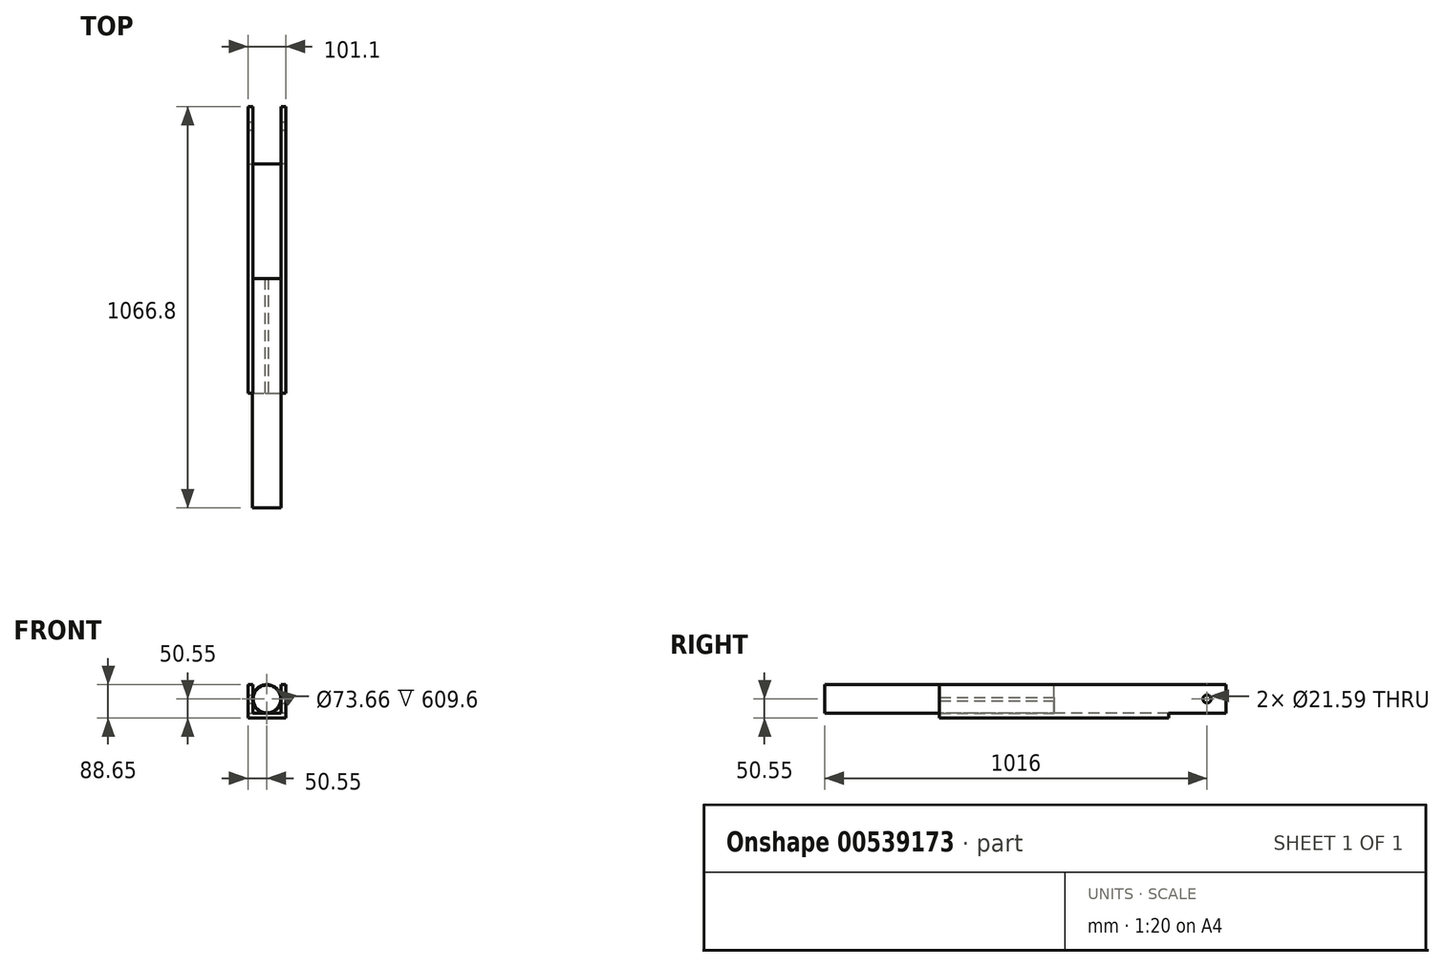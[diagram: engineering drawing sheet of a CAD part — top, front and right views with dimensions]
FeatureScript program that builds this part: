
annotation { "Feature Type Name" : "Feature", "Feature Type Description" : "" }
export const myFeature = defineFeature(function(context is Context, id is Id, definition is map)
    precondition{}
    {
        {
            var Q0;
            Q0=qCreatedBy(makeId("Front.planeOp"),FACE);
            var sketch = newSketch(context, id + "F0", { "sketchPlane" : qUnion([Q0])});
            skCircle(sketch, "E0", {"center": v(0, 0) * mm, "radius": 38.1 * mm});
            skCircle(sketch, "E1", {"center": v(0, 0) * mm, "radius": 36.83 * mm});
            skSolve(sketch);
        }
        {
            var Q0;
            Q0 = qSketchRegion(id + "F0", true);
            extrude(context, id + "F1", {"entities" : qUnion([Q0]), "depth" : 609.6 * mm, "offsetDistance" : 25.4 * mm});
        }
        {
            var Q0;
            Q0=qCreatedBy(makeId("Front.planeOp"),FACE);
            var sketch = newSketch(context, id + "F2", { "sketchPlane" : qUnion([Q0])});
            skLineSegment(sketch, "E2.bottom", {"start": v(-50.55, 38.1) * mm, "end": v(-37.85, 38.1) * mm});
            skLineSegment(sketch, "E2.top", {"start": v(-50.55, -38.1) * mm, "end": v(-37.85, -38.1) * mm});
            skLineSegment(sketch, "E2.left", {"start": v(-50.55, 38.1) * mm, "end": v(-50.55, -38.1) * mm});
            skLineSegment(sketch, "E2.right", {"start": v(-37.85, 38.1) * mm, "end": v(-37.85, -38.1) * mm});
            skLineSegment(sketch, "E3.MirrorCS", {"start": v(37.85, 38.1) * mm, "end": v(37.85, -38.1) * mm});
            skLineSegment(sketch, "E4.MirrorCS", {"start": v(50.55, 38.1) * mm, "end": v(50.55, -38.1) * mm});
            skLineSegment(sketch, "E5.MirrorCS", {"start": v(50.55, 38.1) * mm, "end": v(37.85, 38.1) * mm});
            skLineSegment(sketch, "E6.MirrorCS", {"start": v(50.55, -38.1) * mm, "end": v(37.85, -38.1) * mm});
            skLineSegment(sketch, "E7.bottom", {"start": v(-50.55, -38.1) * mm, "end": v(51.05, -38.1) * mm});
            skLineSegment(sketch, "E7.left", {"start": v(-50.55, -38.1) * mm, "end": v(-50.55, -50.8) * mm});
            skLineSegment(sketch, "E7.right", {"start": v(51.05, -38.1) * mm, "end": v(51.05, -50.8) * mm});
            skSolve(sketch);
        }
        {
            var Q0;
            Q0 = qSketchRegion(id + "F2", true);
            extrude(context, id + "F3", {"entities" : qUnion([Q0]), "operationType" : NewBodyOperationType.ADD, "depth" : 304.8 * mm, "offsetDistance" : 25.4 * mm});
        }
        {
            var Q0;
            Q0 = qSketchRegion(id + "F2", true);
            extrude(context, id + "F4", {"entities" : qUnion([Q0]), "operationType" : NewBodyOperationType.ADD, "depth" : -457.2 * mm, "offsetDistance" : 25.4 * mm});
        }
        {
            var Q0;
            Q0=qCreatedBy(makeId("Front.planeOp"),FACE);
            var sketch = newSketch(context, id + "F5", { "sketchPlane" : qUnion([Q0])});
            skLineSegment(sketch, "E8.bottom", {"start": v(-50.55, -37.85) * mm, "end": v(50.55, -37.85) * mm});
            skLineSegment(sketch, "E8.top", {"start": v(-50.55, -50.55) * mm, "end": v(50.55, -50.55) * mm});
            skLineSegment(sketch, "E8.left", {"start": v(-50.55, -37.85) * mm, "end": v(-50.55, -50.55) * mm});
            skLineSegment(sketch, "E8.right", {"start": v(50.55, -37.85) * mm, "end": v(50.55, -50.55) * mm});
            skSolve(sketch);
        }
        {
            var Q0;
            Q0 = qSketchRegion(id + "F5", true);
            extrude(context, id + "F6", {"entities" : qUnion([Q0]), "operationType" : NewBodyOperationType.ADD, "depth" : 304.8 * mm, "offsetDistance" : 25.4 * mm});
        }
        {
            var Q0;
            Q0 = qSketchRegion(id + "F5", true);
            extrude(context, id + "F7", {"entities" : qUnion([Q0]), "operationType" : NewBodyOperationType.ADD, "depth" : -304.8 * mm, "offsetDistance" : 25.4 * mm});
        }
        {
            var Q0;
            Q0=qCreatedBy(makeId("Right.planeOp"),FACE);
            var sketch = newSketch(context, id + "F8", { "sketchPlane" : qUnion([Q0])});
            skCircle(sketch, "E9", {"center": v(406.4, 0) * mm, "radius": 10.8 * mm});
            skSolve(sketch);
        }
        {
            var Q0;
            Q0 = qSketchRegion(id + "F8", true);
            extrude(context, id + "F9", {"entities" : qUnion([Q0]), "operationType" : NewBodyOperationType.REMOVE, "endBound" : BoundingType.SYMMETRIC, "oppositeDirection" : true, "depth" : 101.6 * mm, "offsetDistance" : 25.4 * mm});
        }
    });
